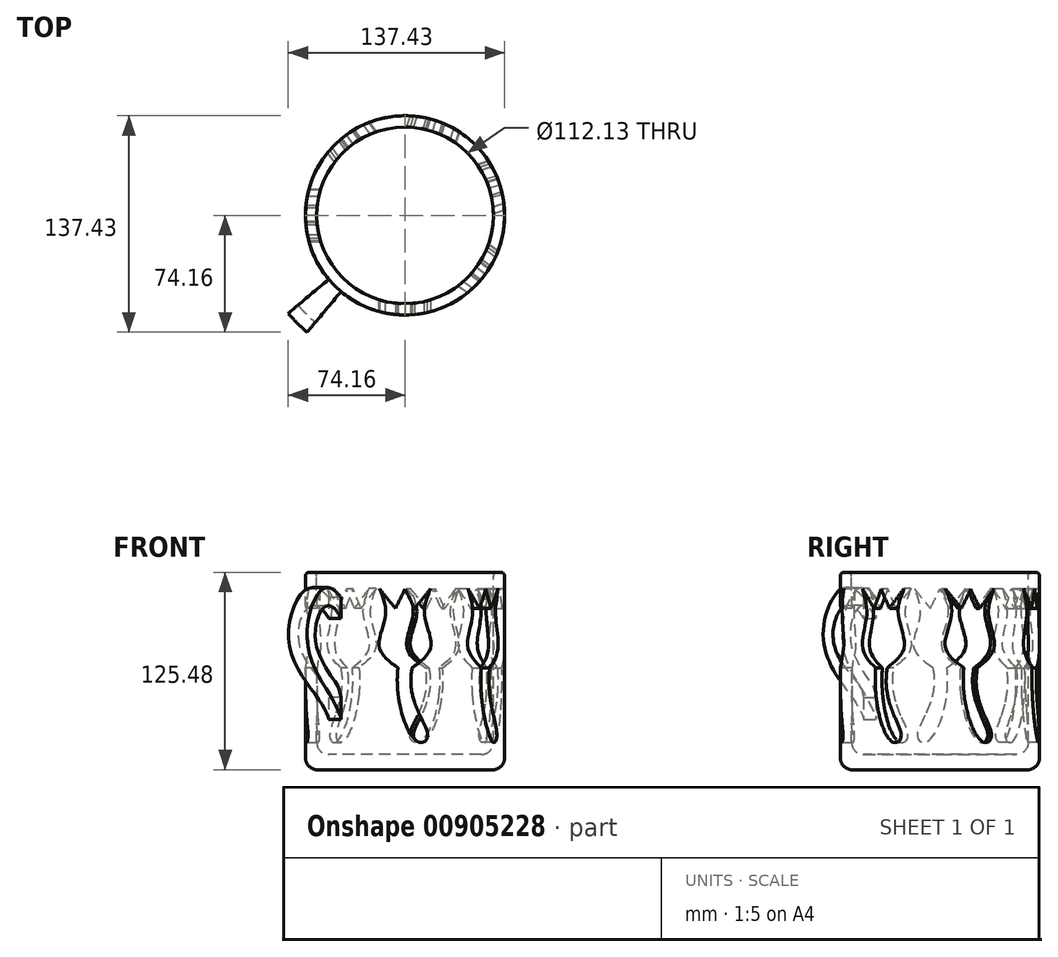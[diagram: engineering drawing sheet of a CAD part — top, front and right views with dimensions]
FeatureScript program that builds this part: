
annotation { "Feature Type Name" : "Feature", "Feature Type Description" : "" }
export const myFeature = defineFeature(function(context is Context, id is Id, definition is map)
    precondition{}
    {
        {
            var Q0;
            Q0=qCreatedBy(makeId("Top.planeOp"),FACE);
            var sketch = newSketch(context, id + "F0", { "sketchPlane" : qUnion([Q0])});
            skCircle(sketch, "E0", {"center": v(0, 0) * mm, "radius": 63.27 * mm});
            skSolve(sketch);
        }
        {
            var Q0;
            Q0=makeQuery(id+"F0.imprint","IMPRINT",FACE,{"disambiguationData":[TD([[makeQuery(id+"F0.imprint","IMPRINT",EDGE,{"derivedFrom":sQuery(id+"F0.wireOp",EDGE,"E0")}),1.0]])]});
            extrude(context, id + "F1", {"entities" : qUnion([Q0]), "depth" : 125.48 * mm, "offsetDistance" : 25.4 * mm});
        }
        {
            var Q0;
            Q0=makeQuery(id+"F1.opExtrude","CAP_FACE",FACE,{"disambiguationData":[OSD([sQuery(id+"F0.wireOp",EDGE,"E0")])],"isStart":false});
            var sketch = newSketch(context, id + "F2", { "sketchPlane" : qUnion([Q0])});
            skCircle(sketch, "E1", {"center": v(0, 0) * mm, "radius": 56.06 * mm});
            skSolve(sketch);
        }
        {
            var Q0;
            Q0=makeQuery(id+"F2.imprint","IMPRINT",FACE,{"disambiguationData":[TD([[makeQuery(id+"F2.imprint","IMPRINT",EDGE,{"derivedFrom":sQuery(id+"F2.wireOp",EDGE,"E1")}),1.0]])]});
            extrude(context, id + "F3", {"entities" : qUnion([Q0]), "operationType" : NewBodyOperationType.REMOVE, "oppositeDirection" : true, "depth" : 115.82 * mm, "offsetDistance" : 25.4 * mm});
        }
        {
            var Q0;
            Q0=qCreatedBy(makeId("Front.planeOp"),FACE);
            cPlane(context, id + "F4", {"entities" : qUnion([Q0]), "cplaneType" : CPlaneType.OFFSET, "offset" : 67.82 * mm, "width" : 152.4 * mm, "height" : 152.4 * mm});
        }
        {
            var Q0;
            Q0=qCreatedBy(makeId("Right.planeOp"),FACE);
            var sketch = newSketch(context, id + "F5", { "sketchPlane" : qUnion([Q0])});
            skLineSegment(sketch, "E2", {"start": v(0, 0) * mm, "end": v(0, 166.4) * mm, "construction": true});
            skSolve(sketch);
        }
        {
            var Q0;
            Q0=qCreatedBy(id+"F4.planeOp",FACE);
            var sketch = newSketch(context, id + "F6", { "sketchPlane" : qUnion([Q0])});
            skLineSegment(sketch, "E3", {"start": v(0, 114.7) * mm, "end": v(-6.1, 102.5) * mm});
            skLineSegment(sketch, "E4", {"start": v(-6.1, 102.5) * mm, "end": v(-16.33, 115.09) * mm});
            skFitSpline(sketch, "E5", {"points": [v(-16.33, 115.09) * mm, v(-12.4, 98.56) * mm, v(-16.33, 78.1) * mm, v(-4.52, 64.72) * mm], "startDerivative": vector(21.42, -49.08) * mm, "endDerivative": vector(49.84, -36.1) * mm});
            skLineSegment(sketch, "E6.MirrorCS", {"start": v(0, 114.7) * mm, "end": v(6.1, 102.5) * mm});
            skLineSegment(sketch, "E7.MirrorCS", {"start": v(6.1, 102.5) * mm, "end": v(16.33, 115.09) * mm});
            skFitSpline(sketch, "E8.MirrorCS", {"points": [v(16.33, 115.09) * mm, v(12.4, 98.56) * mm, v(16.33, 78.1) * mm, v(4.52, 64.72) * mm], "startDerivative": vector(-21.42, -49.08) * mm, "endDerivative": vector(-49.84, -36.1) * mm});
            skFitSpline(sketch, "E9", {"points": [v(-4.52, 64.72) * mm, v(8.85, 17.5) * mm, v(14.36, 21.44) * mm, v(4.52, 64.72) * mm], "startDerivative": vector(-16.45, -150.1) * mm, "endDerivative": vector(33.15, 157.82) * mm});
            skFitSpline(sketch, "E10", {"points": [v(-4.48, 48.75) * mm, v(-17.5, 54.6) * mm, v(-15.54, 43.18) * mm, v(-2.57, 37.95) * mm], "startDerivative": vector(-49.52, 34.36) * mm, "endDerivative": vector(46.19, -0.19) * mm});
            skFitSpline(sketch, "E11", {"points": [v(5.91, 43.18) * mm, v(18.3, 49.87) * mm, v(18.69, 36.1) * mm, v(9.5, 34.44) * mm], "startDerivative": vector(40.97, 41.4) * mm, "endDerivative": vector(-38.76, 5.73) * mm});
            skFitSpline(sketch, "E12.trimOffspring", {"points": [v(-4.52, 64.72) * mm, v(8.85, 17.5) * mm, v(14.36, 21.44) * mm, v(4.52, 64.72) * mm], "startDerivative": vector(-16.45, -150.1) * mm, "endDerivative": vector(33.15, 157.82) * mm});
            skFitSpline(sketch, "E13.trimOffspring", {"points": [v(-4.52, 64.72) * mm, v(8.85, 17.5) * mm, v(14.36, 21.44) * mm, v(4.52, 64.72) * mm], "startDerivative": vector(-16.45, -150.1) * mm, "endDerivative": vector(33.15, 157.82) * mm});
            skSolve(sketch);
        }
        {
            var Q0;
            Q0=makeQuery(id+"F6.imprint","IMPRINT",FACE,{"disambiguationData":[TD([[makeQuery(id+"F6.imprint","IMPRINT",EDGE,{"derivedFrom":sQuery(id+"F6.wireOp",EDGE,"E3")}),1.0]])]});
            extrude(context, id + "F7", {"entities" : qUnion([Q0]), "oppositeDirection" : true, "depth" : 25.4 * mm, "offsetDistance" : 25.4 * mm});
        }
        {
            var Q0;
            Q0=makeQuery(id+"F7.opExtrude","SWEPT_BODY",BODY,{"disambiguationData":[OSD([sQuery(id+"F6.wireOp",EDGE,"E3"),sQuery(id+"F6.wireOp",EDGE,"E4"),sQuery(id+"F6.wireOp",EDGE,"E5"),sQuery(id+"F6.wireOp",EDGE,"E6.MirrorCS"),sQuery(id+"F6.wireOp",EDGE,"E7.MirrorCS"),sQuery(id+"F6.wireOp",EDGE,"E8.MirrorCS"),sQuery(id+"F6.wireOp",EDGE,"E9")])]});
            var Q1;
            Q1=sQuery(id+"F5.wireOp",EDGE,"E2");
            circularPattern(context, id + "F8", {"entities" : qUnion([Q0]), "axis" : qUnion([Q1]), "angle" : 270 * degree, "instanceCount" : 6, "equalSpace" : true});
        }
        {
            var Q0;
            Q0=makeQuery(id+"F7.opExtrude","SWEPT_BODY",BODY,{"disambiguationData":[OSD([sQuery(id+"F6.wireOp",EDGE,"E3"),sQuery(id+"F6.wireOp",EDGE,"E4"),sQuery(id+"F6.wireOp",EDGE,"E5"),sQuery(id+"F6.wireOp",EDGE,"E6.MirrorCS"),sQuery(id+"F6.wireOp",EDGE,"E7.MirrorCS"),sQuery(id+"F6.wireOp",EDGE,"E8.MirrorCS"),sQuery(id+"F6.wireOp",EDGE,"E9")])]});
            var Q1;
            Q1=makeQuery(id+"F8.opPattern","COPY",BODY,{"derivedFrom":makeQuery(id+"F7.opExtrude","SWEPT_BODY",BODY,{"disambiguationData":[OSD([sQuery(id+"F6.wireOp",EDGE,"E3"),sQuery(id+"F6.wireOp",EDGE,"E4"),sQuery(id+"F6.wireOp",EDGE,"E5"),sQuery(id+"F6.wireOp",EDGE,"E6.MirrorCS"),sQuery(id+"F6.wireOp",EDGE,"E7.MirrorCS"),sQuery(id+"F6.wireOp",EDGE,"E8.MirrorCS"),sQuery(id+"F6.wireOp",EDGE,"E9")])]}),"instanceName":"6"});
            var Q2;
            Q2=makeQuery(id+"F8.opPattern","COPY",BODY,{"derivedFrom":makeQuery(id+"F7.opExtrude","SWEPT_BODY",BODY,{"disambiguationData":[OSD([sQuery(id+"F6.wireOp",EDGE,"E3"),sQuery(id+"F6.wireOp",EDGE,"E4"),sQuery(id+"F6.wireOp",EDGE,"E5"),sQuery(id+"F6.wireOp",EDGE,"E6.MirrorCS"),sQuery(id+"F6.wireOp",EDGE,"E7.MirrorCS"),sQuery(id+"F6.wireOp",EDGE,"E8.MirrorCS"),sQuery(id+"F6.wireOp",EDGE,"E9")])]}),"instanceName":"1"});
            var Q3;
            Q3=makeQuery(id+"F8.opPattern","COPY",BODY,{"derivedFrom":makeQuery(id+"F7.opExtrude","SWEPT_BODY",BODY,{"disambiguationData":[OSD([sQuery(id+"F6.wireOp",EDGE,"E3"),sQuery(id+"F6.wireOp",EDGE,"E4"),sQuery(id+"F6.wireOp",EDGE,"E5"),sQuery(id+"F6.wireOp",EDGE,"E6.MirrorCS"),sQuery(id+"F6.wireOp",EDGE,"E7.MirrorCS"),sQuery(id+"F6.wireOp",EDGE,"E8.MirrorCS"),sQuery(id+"F6.wireOp",EDGE,"E9")])]}),"instanceName":"2"});
            var Q4;
            Q4=makeQuery(id+"F8.opPattern","COPY",BODY,{"derivedFrom":makeQuery(id+"F7.opExtrude","SWEPT_BODY",BODY,{"disambiguationData":[OSD([sQuery(id+"F6.wireOp",EDGE,"E3"),sQuery(id+"F6.wireOp",EDGE,"E4"),sQuery(id+"F6.wireOp",EDGE,"E5"),sQuery(id+"F6.wireOp",EDGE,"E6.MirrorCS"),sQuery(id+"F6.wireOp",EDGE,"E7.MirrorCS"),sQuery(id+"F6.wireOp",EDGE,"E8.MirrorCS"),sQuery(id+"F6.wireOp",EDGE,"E9")])]}),"instanceName":"3"});
            var Q5;
            Q5=makeQuery(id+"F8.opPattern","COPY",BODY,{"derivedFrom":makeQuery(id+"F7.opExtrude","SWEPT_BODY",BODY,{"disambiguationData":[OSD([sQuery(id+"F6.wireOp",EDGE,"E3"),sQuery(id+"F6.wireOp",EDGE,"E4"),sQuery(id+"F6.wireOp",EDGE,"E5"),sQuery(id+"F6.wireOp",EDGE,"E6.MirrorCS"),sQuery(id+"F6.wireOp",EDGE,"E7.MirrorCS"),sQuery(id+"F6.wireOp",EDGE,"E8.MirrorCS"),sQuery(id+"F6.wireOp",EDGE,"E9")])]}),"instanceName":"4"});
            var Q6;
            Q6=makeQuery(id+"F8.opPattern","COPY",BODY,{"derivedFrom":makeQuery(id+"F7.opExtrude","SWEPT_BODY",BODY,{"disambiguationData":[OSD([sQuery(id+"F6.wireOp",EDGE,"E3"),sQuery(id+"F6.wireOp",EDGE,"E4"),sQuery(id+"F6.wireOp",EDGE,"E5"),sQuery(id+"F6.wireOp",EDGE,"E6.MirrorCS"),sQuery(id+"F6.wireOp",EDGE,"E7.MirrorCS"),sQuery(id+"F6.wireOp",EDGE,"E8.MirrorCS"),sQuery(id+"F6.wireOp",EDGE,"E9")])]}),"instanceName":"5"});
            var Q7;
            Q7=makeQuery(id+"F1.opExtrude","SWEPT_BODY",BODY,{"disambiguationData":[OSD([sQuery(id+"F0.wireOp",EDGE,"E0")])]});
            booleanBodies(context, id + "F9", {"operationType" : BooleanOperationType.SUBTRACTION, "tools" : qUnion([Q0, Q1, Q2, Q3, Q4, Q5, Q6]), "targets" : qUnion([Q7])});
        }
        {
            var Q0;
            Q0=makeQuery(id+"F1.opExtrude","CAP_FACE",FACE,{"disambiguationData":[OSD([sQuery(id+"F0.wireOp",EDGE,"E0")])],"isStart":false});
            fillet(context, id + "F10", {"entities" : qUnion([Q0]), "radius" : 2.54 * mm, "tangentPropagation" : true, "allowEdgeOverflow" : false});
        }
        {
            var Q0;
            Q0=makeQuery(id+"F1.opExtrude","CAP_EDGE",EDGE,{"disambiguationData":[OSD([sQuery(id+"F0.wireOp",EDGE,"E0")])],"isStart":true});
            var Q1;
            Q1=makeQuery(id+"F3.boolean.opBoolean","COPY",EDGE,{"derivedFrom":makeQuery(id+"F3.opExtrude","CAP_EDGE",EDGE,{"disambiguationData":[OSD([sQuery(id+"F2.wireOp",EDGE,"E1")])],"isStart":false})});
            fillet(context, id + "F11", {"entities" : qUnion([Q0, Q1]), "radius" : 7.62 * mm, "tangentPropagation" : true, "allowEdgeOverflow" : false});
        }
        {
            var Q0;
            Q0=qCreatedBy(makeId("Front.planeOp"),FACE);
            var Q1;
            Q1=sQuery(id+"F5.wireOp",EDGE,"E2");
            cPlane(context, id + "F12", {"entities" : qUnion([Q0, Q1]), "cplaneType" : CPlaneType.LINE_ANGLE, "offset" : 25.4 * mm, "angle" : 45 * degree, "width" : 152.4 * mm, "height" : 152.4 * mm});
        }
        {
            var Q0;
            Q0=qCreatedBy(id+"F12.planeOp",FACE);
            var sketch = newSketch(context, id + "F13", { "sketchPlane" : qUnion([Q0])});
            skFitSpline(sketch, "E14", {"points": [v(63.27, 109.52) * mm, v(82.98, 114.05) * mm, v(96.41, 80.77) * mm, v(71.62, 44.68) * mm, v(63.27, 31.87) * mm], "startDerivative": vector(94.2, 79.62) * mm, "endDerivative": vector(-9.5, -46.57) * mm});
            skLineSegment(sketch, "E15", {"start": v(63.27, 109.52) * mm, "end": v(63.27, 96.15) * mm});
            skFitSpline(sketch, "E16", {"points": [v(63.27, 96.15) * mm, v(80.6, 102.84) * mm, v(88.09, 80.8) * mm, v(69.99, 56.8) * mm, v(63.27, 45.8) * mm], "startDerivative": vector(74.8, 99.2) * mm, "endDerivative": vector(-24.67, -96.75) * mm});
            skLineSegment(sketch, "E17.trimOffspring", {"start": v(63.27, 45.8) * mm, "end": v(63.27, 31.87) * mm});
            skSolve(sketch);
        }
        {
            var Q0;
            Q0 = qSketchRegion(id + "F13", true);
            var Q1;
            Q1=sQuery(id+"F5.wireOp",EDGE,"E2");
            revolve(context, id + "F14", {"operationType" : NewBodyOperationType.ADD, "surfaceOperationType" : NewSurfaceOperationType.NEW, "entities" : qUnion([Q0]), "axis" : qUnion([Q1]), "revolveType" : RevolveType.SYMMETRIC, "angle" : 10 * degree});
        }
    });
